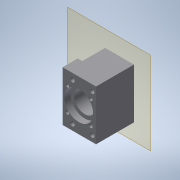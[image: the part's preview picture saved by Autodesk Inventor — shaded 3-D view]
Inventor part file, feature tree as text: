
AUTODESK INVENTOR PART (.ipt)
format: ipt  version: 2022 (Build 260153000, 153)  size: 180,224 bytes
history: native  units: mm
features: reference x12, other x5, sketch x4, extrude x3, plane x1, hole x1
ambient origin geometry x8: Origin, YZ Plane, XZ Plane, XY Plane, X Axis, Y Axis, Z Axis, Center Point
bodies: Volumenkörper1 (feature_tree)
feature tree (26):
  plane  "Arbeitsebene1"
  extrude  "Extrusion1"  Depth=0.5mm
  extrude  "Extrusion2"  Depth=3.0mm
  hole  "Bohrung1"  [1 undecoded]
  extrude  "Extrusion3"  Depth=4.0mm
  sketch  "Skizze1"  dims[d0=0.5mm d1=0.5mm]
  reference  "Referenz1"
  reference  "Referenz2"
  reference  "Referenz3"
  reference  "Referenz4"
  reference  "Referenz5"
  reference  "Referenz6"
  sketch  "Skizze2"  dims[d2=25.0mm d3=0.0mm d4=3.0mm]
  sketch  "Skizze3"  dims[d5=10.0mm d6=25.0mm d7=0.0mm]
  reference  "Referenz7"
  reference  "Referenz8"
  reference  "Referenz9"
  reference  "Referenz10"
  reference  "Referenz11"
  reference  "Referenz12"
  sketch  "Skizze4"  dims[d8=2.5mm d9=6.0mm d10=5.0mm d11=18.0mm d12=90.0deg d13=8.0mm d14=20.594885mm d15=19.0mm d16=4.0mm d17=0.0mm d18=14.0mm]
  other  "Assembly_Cube_Z-Stage_NEMA8_captive_v0.iam"
  other  "30_Cube_Z_Focus_NEMA8_captive_base_v0:1"
  other  "Assembly_Cube_empty_IM_v3:3"
  other  "10_Cube_1x1_IM:1"
  other  "00_Joy-IT-B20SHD4353_NEMA8_captive:1"
note: 1 required parameter value undecoded (feature->parameter linkage not recoverable at this tier; creation-order binding heuristic only, values carry confidence <= 0.55)
